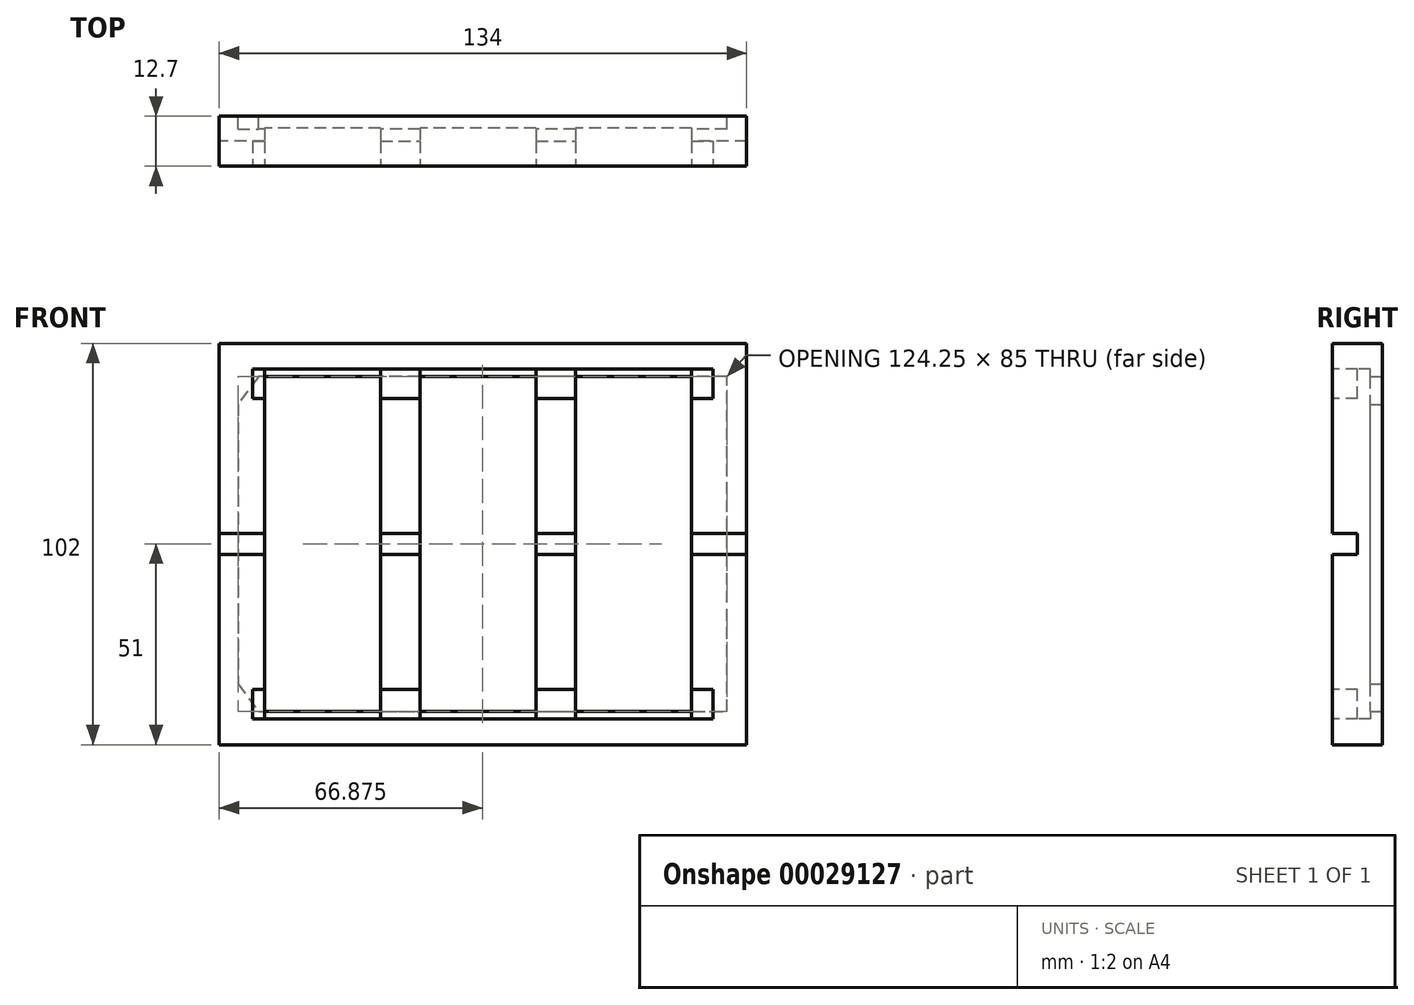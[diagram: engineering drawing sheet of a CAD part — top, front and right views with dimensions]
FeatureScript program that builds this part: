
annotation { "Feature Type Name" : "Feature", "Feature Type Description" : "" }
export const myFeature = defineFeature(function(context is Context, id is Id, definition is map)
    precondition{}
    {
        {
            var Q0;
            Q0=qCreatedBy(makeId("Front.planeOp"),FACE);
            var sketch = newSketch(context, id + "F0", { "sketchPlane" : qUnion([Q0])});
            skLineSegment(sketch, "E0.rect.bottom", {"start": v(67, -51) * mm, "end": v(-67, -51) * mm});
            skLineSegment(sketch, "E0.rect.top", {"start": v(67, 51) * mm, "end": v(-67, 51) * mm});
            skLineSegment(sketch, "E0.rect.left", {"start": v(67, -51) * mm, "end": v(67, 51) * mm});
            skLineSegment(sketch, "E0.rect.right", {"start": v(-67, -51) * mm, "end": v(-67, 51) * mm});
            skPoint(sketch, "E0.rect.middle", {"position": v(0, 0) * mm});
            skLineSegment(sketch, "E1", {"start": v(0, 51) * mm, "end": v(0, -51) * mm, "construction": true});
            skLineSegment(sketch, "E2", {"start": v(-67, 0) * mm, "end": v(67, 0) * mm, "construction": true});
            skSolve(sketch);
        }
        {
            var Q0;
            Q0=makeQuery(id+"F0.imprint","IMPRINT",FACE,{"disambiguationData":[TD([[makeQuery(id+"F0.imprint","IMPRINT",EDGE,{"derivedFrom":sQuery(id+"F0.wireOp",EDGE,"E0.rect.bottom")}),-1.0]])]});
            extrude(context, id + "F1", {"entities" : qUnion([Q0]), "depth" : 12.7 * mm});
        }
        {
            var Q0;
            Q0=makeQuery(id+"F1.opExtrude","CAP_FACE",FACE,{"disambiguationData":[OSD([sQuery(id+"F0.wireOp",EDGE,"E0.rect.bottom"),sQuery(id+"F0.wireOp",EDGE,"E0.rect.top"),sQuery(id+"F0.wireOp",EDGE,"E0.rect.left"),sQuery(id+"F0.wireOp",EDGE,"E0.rect.right")])],"isStart":false});
            var sketch = newSketch(context, id + "F2", { "sketchPlane" : qUnion([Q0])});
            skLineSegment(sketch, "E3.bottom", {"start": v(-16, 39.8) * mm, "end": v(13.5, 39.8) * mm});
            skLineSegment(sketch, "E3.top", {"start": v(-16, -39.8) * mm, "end": v(13.5, -39.8) * mm});
            skLineSegment(sketch, "E3.left", {"start": v(-16, 39.8) * mm, "end": v(-16, -39.8) * mm});
            skLineSegment(sketch, "E3.right", {"start": v(13.5, 39.8) * mm, "end": v(13.5, -39.8) * mm});
            skLineSegment(sketch, "E4.bottom", {"start": v(23.5, 39.8) * mm, "end": v(53, 39.8) * mm});
            skLineSegment(sketch, "E4.top", {"start": v(23.5, -39.8) * mm, "end": v(53, -39.8) * mm});
            skLineSegment(sketch, "E4.left", {"start": v(23.5, 39.8) * mm, "end": v(23.5, -39.8) * mm});
            skLineSegment(sketch, "E4.right", {"start": v(53, 39.8) * mm, "end": v(53, -39.8) * mm});
            skLineSegment(sketch, "E5.bottom", {"start": v(-55.5, 39.8) * mm, "end": v(-26, 39.8) * mm});
            skLineSegment(sketch, "E5.top", {"start": v(-55.5, -39.8) * mm, "end": v(-26, -39.8) * mm});
            skLineSegment(sketch, "E5.left", {"start": v(-55.5, 39.8) * mm, "end": v(-55.5, -39.8) * mm});
            skLineSegment(sketch, "E5.right", {"start": v(-26, 39.8) * mm, "end": v(-26, -39.8) * mm});
            skLineSegment(sketch, "E6", {"start": v(-67, 0) * mm, "end": v(-55.5, 0) * mm, "construction": true});
            skLineSegment(sketch, "E7", {"start": v(53, -16.02) * mm, "end": v(67, -16.02) * mm});
            skSolve(sketch);
        }
        {
            var Q0;
            Q0 = qSketchRegion(id + "F2", true);
            extrude(context, id + "F3", {"entities" : qUnion([Q0]), "operationType" : NewBodyOperationType.REMOVE, "oppositeDirection" : true, "depth" : 12.7 * mm});
        }
        {
            var Q0;
            Q0=makeQuery(id+"F1.opExtrude","CAP_FACE",FACE,{"disambiguationData":[OSD([sQuery(id+"F0.wireOp",EDGE,"E0.rect.bottom"),sQuery(id+"F0.wireOp",EDGE,"E0.rect.top"),sQuery(id+"F0.wireOp",EDGE,"E0.rect.left"),sQuery(id+"F0.wireOp",EDGE,"E0.rect.right")])],"isStart":false});
            var sketch = newSketch(context, id + "F4", { "sketchPlane" : qUnion([Q0])});
            skLineSegment(sketch, "E8.bottom", {"start": v(-58.5, 44.5) * mm, "end": v(58.5, 44.5) * mm});
            skLineSegment(sketch, "E8.top", {"start": v(-58.5, 37) * mm, "end": v(58.5, 37) * mm});
            skLineSegment(sketch, "E8.left", {"start": v(-58.5, 44.5) * mm, "end": v(-58.5, 37) * mm});
            skLineSegment(sketch, "E8.right", {"start": v(58.5, 44.5) * mm, "end": v(58.5, 37) * mm});
            skPoint(sketch, "E9.rect.middle", {"position": v(0, 0) * mm});
            skLineSegment(sketch, "E10.rect.bottom", {"start": v(67, -2.63) * mm, "end": v(-67, -2.63) * mm});
            skLineSegment(sketch, "E10.rect.top", {"start": v(67, 2.62) * mm, "end": v(-67, 2.62) * mm});
            skLineSegment(sketch, "E10.rect.left", {"start": v(67, -2.63) * mm, "end": v(67, 2.62) * mm});
            skLineSegment(sketch, "E10.rect.right", {"start": v(-67, -2.63) * mm, "end": v(-67, 2.62) * mm});
            skPoint(sketch, "E11", {"position": v(-67, 0) * mm});
            skPoint(sketch, "E12", {"position": v(67, 0) * mm});
            skLineSegment(sketch, "E13", {"start": v(-67, 0) * mm, "end": v(67, 0) * mm, "construction": true});
            skLineSegment(sketch, "E14.MirrorCS", {"start": v(-58.5, -44.5) * mm, "end": v(-58.5, -37) * mm});
            skLineSegment(sketch, "E15.MirrorCS", {"start": v(-58.5, -44.5) * mm, "end": v(58.5, -44.5) * mm});
            skLineSegment(sketch, "E16.MirrorCS", {"start": v(58.5, -44.5) * mm, "end": v(58.5, -37) * mm});
            skLineSegment(sketch, "E17.MirrorCS", {"start": v(-58.5, -37) * mm, "end": v(58.5, -37) * mm});
            skLineSegment(sketch, "E18", {"start": v(-58.5, 37) * mm, "end": v(-67, 37) * mm});
            skLineSegment(sketch, "E19", {"start": v(58.5, 37) * mm, "end": v(67, 37) * mm});
            skSolve(sketch);
        }
        {
            var Q0;
            Q0 = qSketchRegion(id + "F4", true);
            extrude(context, id + "F5", {"entities" : qUnion([Q0]), "operationType" : NewBodyOperationType.REMOVE, "oppositeDirection" : true, "depth" : 6.35 * mm});
        }
        {
            var Q0;
            Q0=makeQuery(id+"F1.opExtrude","CAP_FACE",FACE,{"disambiguationData":[OSD([sQuery(id+"F0.wireOp",EDGE,"E0.rect.bottom"),sQuery(id+"F0.wireOp",EDGE,"E0.rect.top"),sQuery(id+"F0.wireOp",EDGE,"E0.rect.left"),sQuery(id+"F0.wireOp",EDGE,"E0.rect.right")])],"isStart":true});
            var sketch = newSketch(context, id + "F6", { "sketchPlane" : qUnion([Q0])});
            skPoint(sketch, "E20.rect.middle", {"position": v(0, 0) * mm});
            skSolve(sketch);
        }
        {
            var Q0;
            Q0=makeQuery(id+"F6.imprint","IMPRINT",FACE,{"disambiguationData":[TD([[makeQuery(id+"F6.imprint","IMPRINT",EDGE,{"derivedFrom":makeQuery(id+"F1.opExtrude","CAP_EDGE",EDGE,{"disambiguationData":[OSD([sQuery(id+"F0.wireOp",EDGE,"E0.rect.bottom")])],"isStart":true})}),1.0]])]});
            var sketch = newSketch(context, id + "F7", { "sketchPlane" : qUnion([Q0])});
            skLineSegment(sketch, "E21", {"start": v(-62, 42.5) * mm, "end": v(57, 42.5) * mm});
            skLineSegment(sketch, "E22", {"start": v(57, 42.5) * mm, "end": v(62.25, 35.5) * mm});
            skLineSegment(sketch, "E23", {"start": v(62.25, 35.5) * mm, "end": v(62.25, -35.5) * mm});
            skLineSegment(sketch, "E24", {"start": v(62.25, -35.5) * mm, "end": v(57, -42.5) * mm});
            skLineSegment(sketch, "E25", {"start": v(57, -42.5) * mm, "end": v(-62, -42.5) * mm});
            skLineSegment(sketch, "E26", {"start": v(-62, -42.5) * mm, "end": v(-62, 42.5) * mm});
            skPoint(sketch, "E27", {"position": v(62.25, 0) * mm});
            skPoint(sketch, "E28", {"position": v(-62, 0) * mm});
            skLineSegment(sketch, "E29.0", {"start": v(-67, 51) * mm, "end": v(67, 51) * mm, "construction": true});
            skLineSegment(sketch, "E30.0", {"start": v(-67, -51) * mm, "end": v(67, -51) * mm, "construction": true});
            skLineSegment(sketch, "E31", {"start": v(2.17, 51) * mm, "end": v(2.17, 42.5) * mm, "construction": true});
            skLineSegment(sketch, "E32", {"start": v(2.69, -42.5) * mm, "end": v(2.69, -51) * mm, "construction": true});
            skSolve(sketch);
        }
        {
            var Q0;
            Q0 = qSketchRegion(id + "F7", true);
            extrude(context, id + "F8", {"entities" : qUnion([Q0]), "operationType" : NewBodyOperationType.REMOVE, "oppositeDirection" : true, "depth" : 3.25 * mm});
        }
        {
            var Q0;
            Q0=makeQuery(id+"F5.boolean.opBoolean","COPY",FACE,{"derivedFrom":makeQuery(id+"F5.opExtrude","CAP_FACE",FACE,{"disambiguationData":[OSD([sQuery(id+"F4.wireOp",EDGE,"E8.bottom"),sQuery(id+"F4.wireOp",EDGE,"E8.top"),sQuery(id+"F4.wireOp",EDGE,"E8.left"),sQuery(id+"F4.wireOp",EDGE,"E8.right")])],"isStart":false})});
            var sketch = newSketch(context, id + "F9", { "sketchPlane" : qUnion([Q0])});
            skLineSegment(sketch, "E33.bottom", {"start": v(-16, 39.8) * mm, "end": v(13.5, 39.8) * mm});
            skLineSegment(sketch, "E33.top", {"start": v(-16, 44.5) * mm, "end": v(13.5, 44.5) * mm});
            skLineSegment(sketch, "E33.left", {"start": v(-16, 39.8) * mm, "end": v(-16, 44.5) * mm});
            skLineSegment(sketch, "E33.right", {"start": v(13.5, 39.8) * mm, "end": v(13.5, 44.5) * mm});
            skLineSegment(sketch, "E34.bottom", {"start": v(23.5, 39.8) * mm, "end": v(53, 39.8) * mm});
            skLineSegment(sketch, "E34.top", {"start": v(23.5, 44.5) * mm, "end": v(53, 44.5) * mm});
            skLineSegment(sketch, "E34.left", {"start": v(23.5, 39.8) * mm, "end": v(23.5, 44.5) * mm});
            skLineSegment(sketch, "E34.right", {"start": v(53, 39.8) * mm, "end": v(53, 44.5) * mm});
            skLineSegment(sketch, "E35.bottom", {"start": v(-55.5, 39.8) * mm, "end": v(-26, 39.8) * mm});
            skLineSegment(sketch, "E35.top", {"start": v(-55.5, 44.5) * mm, "end": v(-26, 44.5) * mm});
            skLineSegment(sketch, "E35.left", {"start": v(-55.5, 39.8) * mm, "end": v(-55.5, 44.5) * mm});
            skLineSegment(sketch, "E35.right", {"start": v(-26, 39.8) * mm, "end": v(-26, 44.5) * mm});
            skPoint(sketch, "E36", {"position": v(-66.9, 0) * mm});
            skPoint(sketch, "E37", {"position": v(66.96, 0) * mm});
            skLineSegment(sketch, "E38", {"start": v(-66.9, 0) * mm, "end": v(66.96, 0) * mm, "construction": true});
            skLineSegment(sketch, "E39.MirrorCS", {"start": v(-55.5, -44.5) * mm, "end": v(-26, -44.5) * mm});
            skLineSegment(sketch, "E40.MirrorCS", {"start": v(-55.5, -39.8) * mm, "end": v(-55.5, -44.5) * mm});
            skLineSegment(sketch, "E41.MirrorCS", {"start": v(-55.5, -39.8) * mm, "end": v(-26, -39.8) * mm});
            skLineSegment(sketch, "E42.MirrorCS", {"start": v(-26, -39.8) * mm, "end": v(-26, -44.5) * mm});
            skLineSegment(sketch, "E43.MirrorCS", {"start": v(-16, -44.5) * mm, "end": v(13.5, -44.5) * mm});
            skLineSegment(sketch, "E44.MirrorCS", {"start": v(-16, -39.8) * mm, "end": v(-16, -44.5) * mm});
            skLineSegment(sketch, "E45.MirrorCS", {"start": v(13.5, -39.8) * mm, "end": v(13.5, -44.5) * mm});
            skLineSegment(sketch, "E46.MirrorCS", {"start": v(-16, -39.8) * mm, "end": v(13.5, -39.8) * mm});
            skLineSegment(sketch, "E47.MirrorCS", {"start": v(23.5, -44.5) * mm, "end": v(53, -44.5) * mm});
            skLineSegment(sketch, "E48.MirrorCS", {"start": v(23.5, -39.8) * mm, "end": v(23.5, -44.5) * mm});
            skLineSegment(sketch, "E49.MirrorCS", {"start": v(23.5, -39.8) * mm, "end": v(53, -39.8) * mm});
            skLineSegment(sketch, "E50.MirrorCS", {"start": v(53, -39.8) * mm, "end": v(53, -44.5) * mm});
            skSolve(sketch);
        }
        {
            var Q0;
            Q0 = qSketchRegion(id + "F9", true);
            extrude(context, id + "F10", {"entities" : qUnion([Q0]), "operationType" : NewBodyOperationType.REMOVE, "oppositeDirection" : true, "depth" : 3.3 * mm});
        }
    });
